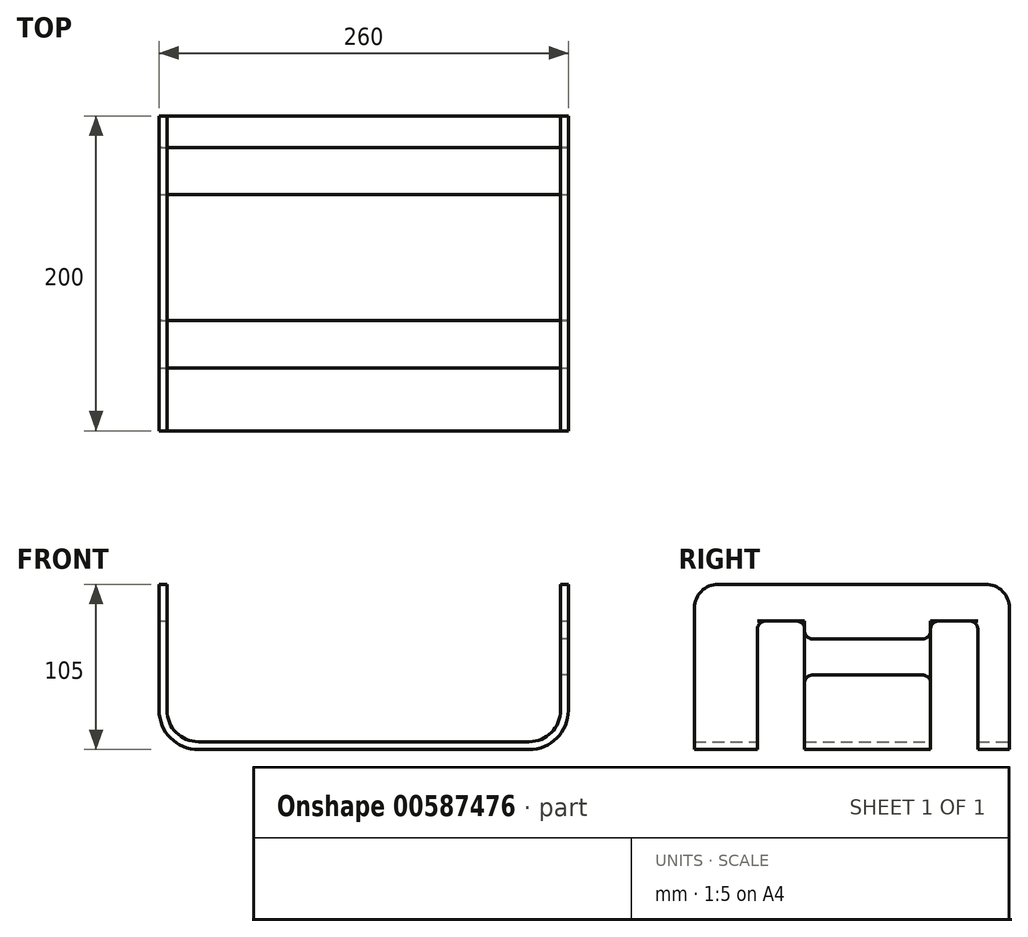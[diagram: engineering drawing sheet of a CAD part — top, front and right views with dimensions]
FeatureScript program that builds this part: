
annotation { "Feature Type Name" : "Feature", "Feature Type Description" : "" }
export const myFeature = defineFeature(function(context is Context, id is Id, definition is map)
    precondition{}
    {
        {
            var Q0;
            Q0=qCreatedBy(makeId("Front.planeOp"),FACE);
            var sketch = newSketch(context, id + "F0", { "sketchPlane" : qUnion([Q0])});
            skLineSegment(sketch, "E0", {"start": v(-127.55, 43.5) * mm, "end": v(-127.55, -36.5) * mm});
            skLineSegment(sketch, "E1", {"start": v(-107.55, -56.5) * mm, "end": v(102.45, -56.5) * mm});
            skLineSegment(sketch, "E2", {"start": v(122.45, -36.5) * mm, "end": v(122.45, 43.5) * mm});
            skPoint(sketch, "E3.visualSharp", {"position": v(-127.55, -56.5) * mm});
            skArc(sketch, "E3.filletArc", {"start": v(-127.55, -36.5) * mm, "mid": v(-121.7, -50.64) * mm, "end": v(-107.55, -56.5) * mm});
            skPoint(sketch, "E4.visualSharp", {"position": v(122.45, -56.5) * mm});
            skArc(sketch, "E4.filletArc", {"start": v(102.45, -56.5) * mm, "mid": v(116.59, -50.64) * mm, "end": v(122.45, -36.5) * mm});
            skLineSegment(sketch, "E5.0", {"start": v(127.45, -36.5) * mm, "end": v(127.45, 43.5) * mm});
            skLineSegment(sketch, "E5.1", {"start": v(-132.55, 43.5) * mm, "end": v(-132.55, -36.5) * mm});
            skArc(sketch, "E5.2", {"start": v(-132.55, -36.5) * mm, "mid": v(-125.23, -54.18) * mm, "end": v(-107.55, -61.5) * mm});
            skLineSegment(sketch, "E5.3", {"start": v(-107.55, -61.5) * mm, "end": v(102.45, -61.5) * mm});
            skArc(sketch, "E5.4", {"start": v(102.45, -61.5) * mm, "mid": v(120.12, -54.18) * mm, "end": v(127.45, -36.5) * mm});
            skLineSegment(sketch, "E6", {"start": v(-132.55, 43.5) * mm, "end": v(-127.55, 43.5) * mm});
            skLineSegment(sketch, "E7", {"start": v(122.45, 43.5) * mm, "end": v(127.45, 43.5) * mm});
            skSolve(sketch);
        }
        {
            var Q0;
            Q0=qCreatedBy(makeId("Right.planeOp"),FACE);
            cPlane(context, id + "F1", {"entities" : qUnion([Q0]), "cplaneType" : CPlaneType.OFFSET, "offset" : 200 * mm, "width" : 150 * mm, "height" : 150 * mm});
        }
        {
            var Q0;
            Q0=makeQuery(id+"F0.imprint","IMPRINT",FACE,{"disambiguationData":[TD([[makeQuery(id+"F0.imprint","IMPRINT",EDGE,{"derivedFrom":sQuery(id+"F0.wireOp",EDGE,"E0")}),-1.0]])]});
            extrude(context, id + "F2", {"entities" : qUnion([Q0]), "depth" : 200 * mm, "offsetDistance" : 25 * mm});
        }
        {
            var Q0;
            Q0=qCreatedBy(id+"F1.planeOp",FACE);
            var sketch = newSketch(context, id + "F3", { "sketchPlane" : qUnion([Q0])});
            skLineSegment(sketch, "E8", {"start": v(-160, 20.09) * mm, "end": v(-160, -79.91) * mm});
            skLineSegment(sketch, "E9", {"start": v(-160, -79.91) * mm, "end": v(-130, -79.91) * mm});
            skLineSegment(sketch, "E10", {"start": v(-20, -79.91) * mm, "end": v(-20, 20.09) * mm});
            skLineSegment(sketch, "E11", {"start": v(-20, 20.09) * mm, "end": v(-50, 20.09) * mm});
            skLineSegment(sketch, "E12", {"start": v(-50, 20.09) * mm, "end": v(-50, -79.91) * mm});
            skLineSegment(sketch, "E13", {"start": v(-130, -79.91) * mm, "end": v(-130, 20.09) * mm});
            skLineSegment(sketch, "E14", {"start": v(-130, 20.09) * mm, "end": v(-160, 20.09) * mm});
            skLineSegment(sketch, "E15.filletArc", {"start": v(-130, -79.91) * mm, "end": v(-130, -79.91) * mm});
            skLineSegment(sketch, "E16", {"start": v(-50, -79.91) * mm, "end": v(-20, -79.91) * mm});
            skLineSegment(sketch, "E17.filletArc", {"start": v(-20, -79.91) * mm, "end": v(-20, -79.91) * mm});
            skSolve(sketch);
        }
        {
            var Q0;
            Q0=makeQuery(id+"F3.imprint","IMPRINT",FACE,{"disambiguationData":[TD([[makeQuery(id+"F3.imprint","IMPRINT",EDGE,{"derivedFrom":sQuery(id+"F3.wireOp",EDGE,"E8")}),1.0]])]});
            var Q1;
            Q1=makeQuery(id+"F3.imprint","IMPRINT",FACE,{"disambiguationData":[TD([[makeQuery(id+"F3.imprint","IMPRINT",EDGE,{"derivedFrom":sQuery(id+"F3.wireOp",EDGE,"E10")}),1.0]])]});
            extrude(context, id + "F4", {"entities" : qUnion([Q0, Q1]), "oppositeDirection" : true, "depth" : 500 * mm, "offsetDistance" : 25 * mm});
        }
        {
            var Q0;
            Q0=makeQuery(id+"F4.opExtrude","SWEPT_BODY",BODY,{"disambiguationData":[OSD([sQuery(id+"F3.wireOp",EDGE,"E8"),sQuery(id+"F3.wireOp",EDGE,"E9"),sQuery(id+"F3.wireOp",EDGE,"E10"),sQuery(id+"F3.wireOp",EDGE,"E11"),sQuery(id+"F3.wireOp",EDGE,"E12"),sQuery(id+"F3.wireOp",EDGE,"sOlcA3gc-G1YB-Knjk-OlmM-VOpdweEhVf90"),sQuery(id+"F3.wireOp",EDGE,"E13"),sQuery(id+"F3.wireOp",EDGE,"E14")])]});
            var Q1;
            Q1=makeQuery(id+"F4.opExtrude","SWEPT_BODY",BODY,{"disambiguationData":[OSD([sQuery(id+"F3.wireOp",EDGE,"E10"),sQuery(id+"F3.wireOp",EDGE,"E11"),sQuery(id+"F3.wireOp",EDGE,"E12"),sQuery(id+"F3.wireOp",EDGE,"E16")])]});
            var Q2;
            Q2=makeQuery(id+"F2.opExtrude","SWEPT_BODY",BODY,{"disambiguationData":[OSD([sQuery(id+"F0.wireOp",EDGE,"E0"),sQuery(id+"F0.wireOp",EDGE,"E1"),sQuery(id+"F0.wireOp",EDGE,"E2"),sQuery(id+"F0.wireOp",EDGE,"E3.filletArc"),sQuery(id+"F0.wireOp",EDGE,"E4.filletArc"),sQuery(id+"F0.wireOp",EDGE,"E5.0"),sQuery(id+"F0.wireOp",EDGE,"E5.1"),sQuery(id+"F0.wireOp",EDGE,"E5.2"),sQuery(id+"F0.wireOp",EDGE,"E5.3"),sQuery(id+"F0.wireOp",EDGE,"E5.4"),sQuery(id+"F0.wireOp",EDGE,"E6"),sQuery(id+"F0.wireOp",EDGE,"E7")])]});
            booleanBodies(context, id + "F5", {"operationType" : BooleanOperationType.SUBTRACTION, "tools" : qUnion([Q0, Q1]), "targets" : qUnion([Q2])});
        }
        {
            var Q0;
            Q0=makeQuery(id+"F2.opExtrude","CAP_EDGE",EDGE,{"disambiguationData":[OSD([sQuery(id+"F0.wireOp",EDGE,"E6")])],"isStart":false});
            var Q1;
            Q1=makeQuery(id+"F2.opExtrude","CAP_EDGE",EDGE,{"disambiguationData":[OSD([sQuery(id+"F0.wireOp",EDGE,"E6")])],"isStart":true});
            var Q2;
            Q2=makeQuery(id+"F2.opExtrude","CAP_EDGE",EDGE,{"disambiguationData":[OSD([sQuery(id+"F0.wireOp",EDGE,"E7")])],"isStart":false});
            var Q3;
            Q3=makeQuery(id+"F2.opExtrude","CAP_EDGE",EDGE,{"disambiguationData":[OSD([sQuery(id+"F0.wireOp",EDGE,"E7")])],"isStart":true});
            fillet(context, id + "F6", {"entities" : qUnion([Q0, Q1, Q2, Q3]), "radius" : 15 * mm, "tangentPropagation" : true, "allowEdgeOverflow" : false});
        }
        {
            var Q0;
            {var subQ0=sQuery(id+"F3.wireOp",EDGE,"E10");var subQ1=sQuery(id+"F3.wireOp",EDGE,"E11");Q0=makeQuery(id+"F5.opBoolean","COPY",EDGE,{"disambiguationData":[TD([makeQuery(id+"F2.opExtrude","SWEPT_FACE",FACE,{"disambiguationData":[OSD([sQuery(id+"F0.wireOp",EDGE,"E2")])]})])],"derivedFrom":makeQuery(id+"F4.opExtrude","SWEPT_EDGE",EDGE,{"disambiguationData":[OSD([subQ0,subQ1])]})});}
            var Q1;
            {var subQ0=sQuery(id+"F3.wireOp",EDGE,"E11");var subQ1=sQuery(id+"F3.wireOp",EDGE,"E12");Q1=makeQuery(id+"F5.opBoolean","COPY",EDGE,{"disambiguationData":[TD([makeQuery(id+"F2.opExtrude","SWEPT_FACE",FACE,{"disambiguationData":[OSD([sQuery(id+"F0.wireOp",EDGE,"E2")])]})])],"derivedFrom":makeQuery(id+"F4.opExtrude","SWEPT_EDGE",EDGE,{"disambiguationData":[OSD([subQ0,subQ1])]})});}
            fillet(context, id + "F7", {"entities" : qUnion([Q0, Q1]), "radius" : 5 * mm, "tangentPropagation" : true, "allowEdgeOverflow" : false});
        }
        {
            var Q0;
            Q0=qCreatedBy(id+"F1.planeOp",FACE);
            var sketch = newSketch(context, id + "F8", { "sketchPlane" : qUnion([Q0])});
            skLineSegment(sketch, "E18.bottom", {"start": v(-142.25, 8.8) * mm, "end": v(-41.14, 8.8) * mm});
            skLineSegment(sketch, "E18.top", {"start": v(-142.25, -14.18) * mm, "end": v(-41.14, -14.18) * mm});
            skLineSegment(sketch, "E18.left", {"start": v(-142.25, 8.8) * mm, "end": v(-142.25, -14.18) * mm});
            skLineSegment(sketch, "E18.right", {"start": v(-41.14, 8.8) * mm, "end": v(-41.14, -14.18) * mm});
            skSolve(sketch);
        }
        {
            var Q0;
            Q0=makeQuery(id+"F8.imprint","IMPRINT",FACE,{"disambiguationData":[TD([[makeQuery(id+"F8.imprint","IMPRINT",EDGE,{"derivedFrom":sQuery(id+"F8.wireOp",EDGE,"E18.bottom")}),-1.0]])]});
            extrude(context, id + "F9", {"entities" : qUnion([Q0]), "operationType" : NewBodyOperationType.REMOVE, "oppositeDirection" : true, "depth" : 200 * mm, "offsetDistance" : 25 * mm});
        }
        {
            var Q0;
            Q0=makeQuery(id+"F9.boolean.opBoolean","INTERSECT",EDGE,{"derivedFrom":[makeQuery(id+"F5.opBoolean","COPY",FACE,{"derivedFrom":makeQuery(id+"F4.opExtrude","SWEPT_FACE",FACE,{"disambiguationData":[OSD([sQuery(id+"F3.wireOp",EDGE,"E12")])]})}),makeQuery(id+"F9.opExtrude","SWEPT_FACE",FACE,{"disambiguationData":[OSD([sQuery(id+"F8.wireOp",EDGE,"E18.top")])]})]});
            var Q1;
            Q1=makeQuery(id+"F9.boolean.opBoolean","INTERSECT",EDGE,{"derivedFrom":[makeQuery(id+"F5.opBoolean","COPY",FACE,{"derivedFrom":makeQuery(id+"F4.opExtrude","SWEPT_FACE",FACE,{"disambiguationData":[OSD([sQuery(id+"F3.wireOp",EDGE,"E12")])]})}),makeQuery(id+"F9.opExtrude","SWEPT_FACE",FACE,{"disambiguationData":[OSD([sQuery(id+"F8.wireOp",EDGE,"E18.bottom")])]})]});
            var Q2;
            Q2=makeQuery(id+"F9.boolean.opBoolean","INTERSECT",EDGE,{"derivedFrom":[makeQuery(id+"F5.opBoolean","COPY",FACE,{"derivedFrom":makeQuery(id+"F4.opExtrude","SWEPT_FACE",FACE,{"disambiguationData":[OSD([sQuery(id+"F3.wireOp",EDGE,"E13")])]})}),makeQuery(id+"F9.opExtrude","SWEPT_FACE",FACE,{"disambiguationData":[OSD([sQuery(id+"F8.wireOp",EDGE,"E18.bottom")])]})]});
            var Q3;
            Q3=makeQuery(id+"F9.boolean.opBoolean","INTERSECT",EDGE,{"derivedFrom":[makeQuery(id+"F5.opBoolean","COPY",FACE,{"derivedFrom":makeQuery(id+"F4.opExtrude","SWEPT_FACE",FACE,{"disambiguationData":[OSD([sQuery(id+"F3.wireOp",EDGE,"E13")])]})}),makeQuery(id+"F9.opExtrude","SWEPT_FACE",FACE,{"disambiguationData":[OSD([sQuery(id+"F8.wireOp",EDGE,"E18.top")])]})]});
            var Q4;
            {var subQ0=sQuery(id+"F3.wireOp",EDGE,"E13");var subQ1=sQuery(id+"F3.wireOp",EDGE,"E14");Q4=makeQuery(id+"F5.opBoolean","COPY",EDGE,{"disambiguationData":[TD([makeQuery(id+"F2.opExtrude","SWEPT_FACE",FACE,{"disambiguationData":[OSD([sQuery(id+"F0.wireOp",EDGE,"E2")])]})])],"derivedFrom":makeQuery(id+"F4.opExtrude","SWEPT_EDGE",EDGE,{"disambiguationData":[OSD([subQ0,subQ1])]})});}
            var Q5;
            {var subQ0=sQuery(id+"F3.wireOp",EDGE,"E8");var subQ1=sQuery(id+"F3.wireOp",EDGE,"E14");Q5=makeQuery(id+"F5.opBoolean","COPY",EDGE,{"disambiguationData":[TD([makeQuery(id+"F2.opExtrude","SWEPT_FACE",FACE,{"disambiguationData":[OSD([sQuery(id+"F0.wireOp",EDGE,"E2")])]})])],"derivedFrom":makeQuery(id+"F4.opExtrude","SWEPT_EDGE",EDGE,{"disambiguationData":[OSD([subQ0,subQ1])]})});}
            fillet(context, id + "F10", {"entities" : qUnion([Q0, Q1, Q2, Q3, Q4, Q5]), "radius" : 5 * mm, "tangentPropagation" : true, "allowEdgeOverflow" : false});
        }
    });
